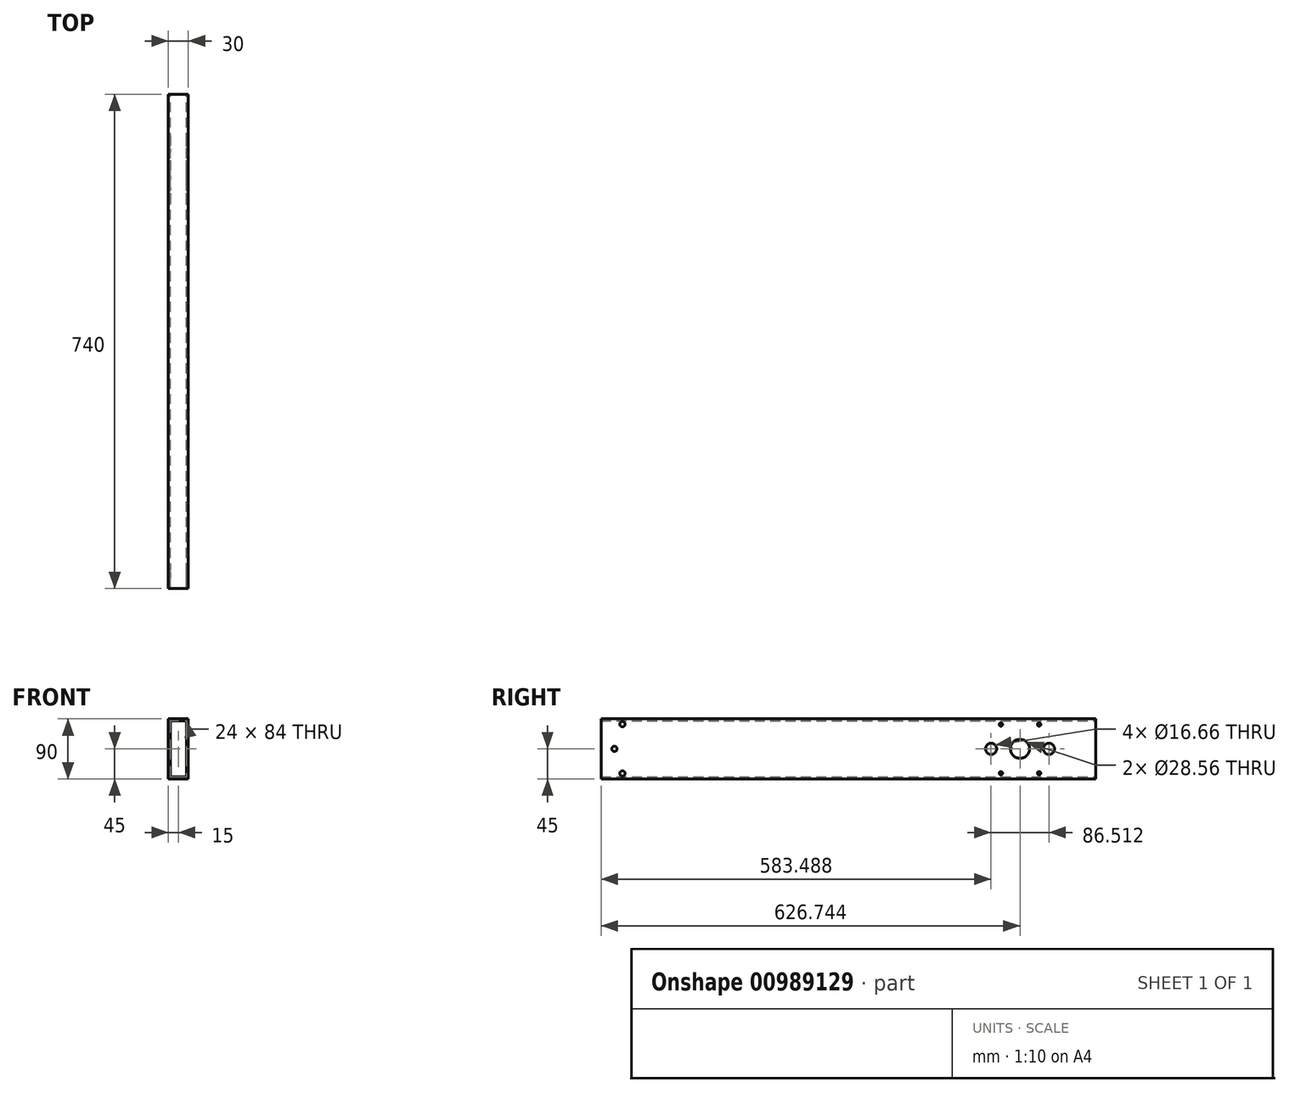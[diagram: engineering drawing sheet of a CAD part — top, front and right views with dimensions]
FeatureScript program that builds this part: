
annotation { "Feature Type Name" : "Feature", "Feature Type Description" : "" }
export const myFeature = defineFeature(function(context is Context, id is Id, definition is map)
    precondition{}
    {
        {
            var Q0;
            Q0=qCreatedBy(makeId("Front.planeOp"),FACE);
            var sketch = newSketch(context, id + "F0", { "sketchPlane" : qUnion([Q0])});
            skLineSegment(sketch, "E0.bottom", {"start": v(15, 45) * mm, "end": v(-15, 45) * mm});
            skLineSegment(sketch, "E0.top", {"start": v(15, -45) * mm, "end": v(-15, -45) * mm});
            skLineSegment(sketch, "E0.left", {"start": v(15, 45) * mm, "end": v(15, -45) * mm});
            skLineSegment(sketch, "E0.right", {"start": v(-15, 45) * mm, "end": v(-15, -45) * mm});
            skPoint(sketch, "E0.middle", {"position": v(0, 0) * mm});
            skSolve(sketch);
        }
        {
            var Q0;
            Q0=qSketchRegion(id+"F0",true);
            extrude(context, id + "F1", {"entities" : qUnion([Q0]), "endBound" : BoundingType.SYMMETRIC, "depth" : 740 * mm, "offsetDistance" : 25.4 * mm});
        }
        {
            var Q0;
            Q0=makeQuery(id+"F1.opExtrude","CAP_FACE",FACE,{"disambiguationData":[OSD([sQuery(id+"F0.wireOp",EDGE,"E0.bottom"),sQuery(id+"F0.wireOp",EDGE,"E0.top"),sQuery(id+"F0.wireOp",EDGE,"E0.left"),sQuery(id+"F0.wireOp",EDGE,"E0.right")])],"isStart":false});
            var Q1;
            Q1=makeQuery(id+"F1.opExtrude","CAP_FACE",FACE,{"disambiguationData":[OSD([sQuery(id+"F0.wireOp",EDGE,"E0.bottom"),sQuery(id+"F0.wireOp",EDGE,"E0.top"),sQuery(id+"F0.wireOp",EDGE,"E0.left"),sQuery(id+"F0.wireOp",EDGE,"E0.right")])],"isStart":true});
            shell(context, id + "F2", {"entities" : qUnion([Q0, Q1]), "thickness" : 3 * mm});
        }
        {
            var Q0;
            Q0=makeQuery(id+"F1.opExtrude","SWEPT_FACE",FACE,{"disambiguationData":[OSD([sQuery(id+"F0.wireOp",EDGE,"E0.left")])]});
            var sketch = newSketch(context, id + "F3", { "sketchPlane" : qUnion([Q0])});
            skCircle(sketch, "E1.0", {"center": v(228.17, 36.51) * mm, "radius": 2.55 * mm});
            skCircle(sketch, "E1.1", {"center": v(228.17, -36.51) * mm, "radius": 2.55 * mm});
            skCircle(sketch, "E1.2", {"center": v(285.32, -36.51) * mm, "radius": 2.55 * mm});
            skCircle(sketch, "E1.3", {"center": v(285.32, 36.51) * mm, "radius": 2.55 * mm});
            skCircle(sketch, "E2.0", {"center": v(256.74, 0) * mm, "radius": 14.28 * mm});
            skCircle(sketch, "E3.0", {"center": v(213.49, 0) * mm, "radius": 8.33 * mm});
            skCircle(sketch, "E4.0", {"center": v(300, 0) * mm, "radius": 8.33 * mm});
            skLineSegment(sketch, "E5", {"start": v(213.49, 0) * mm, "end": v(256.74, 0) * mm, "construction": true});
            skLineSegment(sketch, "E6", {"start": v(256.74, 0) * mm, "end": v(300, 0) * mm, "construction": true});
            skLineSegment(sketch, "E7.bottom", {"start": v(228.17, 36.51) * mm, "end": v(285.32, 36.51) * mm, "construction": true});
            skLineSegment(sketch, "E7.top", {"start": v(228.17, -36.51) * mm, "end": v(285.32, -36.51) * mm, "construction": true});
            skLineSegment(sketch, "E7.left", {"start": v(228.17, 36.51) * mm, "end": v(228.17, -36.51) * mm, "construction": true});
            skLineSegment(sketch, "E7.right", {"start": v(285.32, 36.51) * mm, "end": v(285.32, -36.51) * mm, "construction": true});
            skLineSegment(sketch, "E8", {"start": v(228.17, 36.51) * mm, "end": v(285.32, -36.51) * mm, "construction": true});
            skLineSegment(sketch, "E9", {"start": v(370, 0) * mm, "end": v(-370, 0) * mm, "construction": true});
            skSolve(sketch);
        }
        {
            var Q0;
            Q0 = qSketchRegion(id + "F3", true);
            extrude(context, id + "F4", {"entities" : qUnion([Q0]), "operationType" : NewBodyOperationType.REMOVE, "endBound" : BoundingType.THROUGH_ALL, "oppositeDirection" : true, "depth" : 25 * mm, "offsetDistance" : 25 * mm});
        }
        {
            var Q0;
            Q0=makeQuery(id+"F1.opExtrude","SWEPT_FACE",FACE,{"disambiguationData":[OSD([sQuery(id+"F0.wireOp",EDGE,"E0.left")])]});
            var sketch = newSketch(context, id + "F5", { "sketchPlane" : qUnion([Q0])});
            skLineSegment(sketch, "E10", {"start": v(-330, 0) * mm, "end": v(-370, 0) * mm, "construction": true});
            skCircle(sketch, "E11", {"center": v(-338, 37) * mm, "radius": 4 * mm});
            skCircle(sketch, "E12", {"center": v(-350, 0) * mm, "radius": 4 * mm});
            skCircle(sketch, "E13", {"center": v(-338, -37) * mm, "radius": 4 * mm});
            skSolve(sketch);
        }
        {
            var Q0;
            Q0 = qSketchRegion(id + "F5", true);
            extrude(context, id + "F6", {"entities" : qUnion([Q0]), "operationType" : NewBodyOperationType.REMOVE, "endBound" : BoundingType.THROUGH_ALL, "oppositeDirection" : true, "depth" : 25 * mm, "offsetDistance" : 25 * mm});
        }
    });
